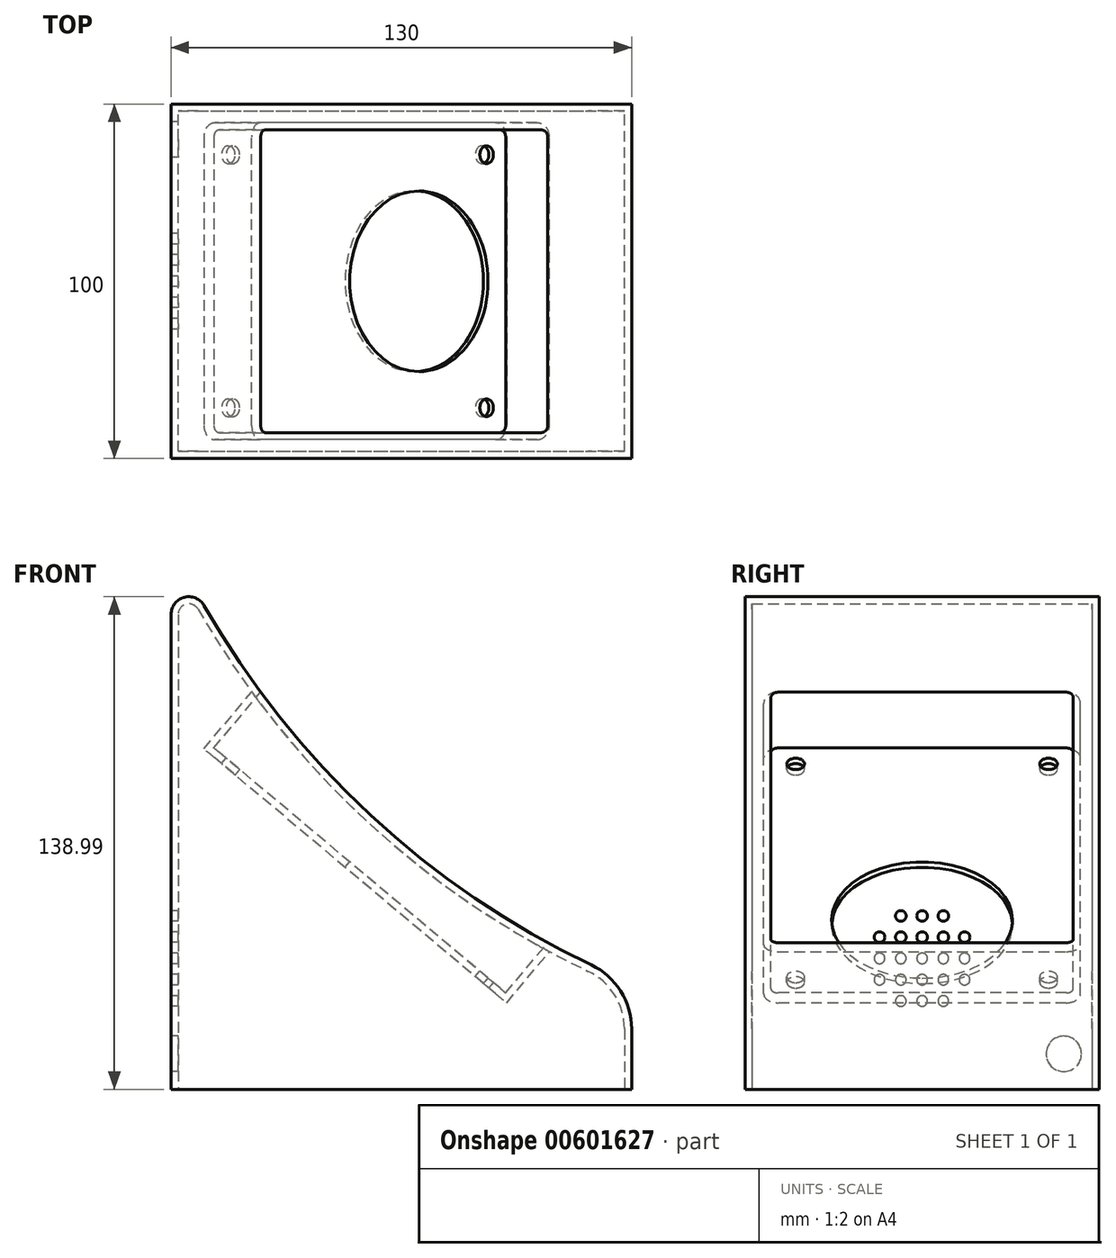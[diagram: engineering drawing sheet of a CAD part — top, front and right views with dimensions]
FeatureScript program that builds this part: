
annotation { "Feature Type Name" : "Feature", "Feature Type Description" : "" }
export const myFeature = defineFeature(function(context is Context, id is Id, definition is map)
    precondition{}
    {
        {
            var Q0;
            Q0=qCreatedBy(makeId("Front.planeOp"),FACE);
            var sketch = newSketch(context, id + "F0", { "sketchPlane" : qUnion([Q0])});
            skLineSegment(sketch, "E0", {"start": v(-84.02, -67.29) * mm, "end": v(45.98, -67.29) * mm});
            skPoint(sketch, "E1.visualSharp", {"position": v(-84.02, 87.14) * mm});
            skPoint(sketch, "E2.visualSharp", {"position": v(45.98, -37.29) * mm});
            skArc(sketch, "E3", {"start": v(-74.68, 69.19) * mm, "mid": v(-23.15, 5.98) * mm, "end": v(45.98, -37.29) * mm});
            skLineSegment(sketch, "E4", {"start": v(-84.02, 66.7) * mm, "end": v(-84.02, -67.29) * mm});
            skLineSegment(sketch, "E5", {"start": v(45.98, -37.29) * mm, "end": v(45.98, -67.29) * mm});
            skArc(sketch, "E6.filletArc", {"start": v(-74.68, 69.19) * mm, "mid": v(-80.3, 71.53) * mm, "end": v(-84.02, 66.7) * mm});
            skSolve(sketch);
        }
        {
            var Q0;
            Q0=makeQuery(id+"F0.imprint","IMPRINT",FACE,{"disambiguationData":[TD([[makeQuery(id+"F0.imprint","IMPRINT",EDGE,{"derivedFrom":sQuery(id+"F0.wireOp",EDGE,"E0")}),1.0]])]});
            extrude(context, id + "F1", {"entities" : qUnion([Q0]), "endBound" : BoundingType.SYMMETRIC, "depth" : 100 * mm});
        }
        {
            var Q0;
            Q0=makeQuery(id+"F1.opExtrude","SWEPT_EDGE",EDGE,{"disambiguationData":[OSD([sQuery(id+"F0.wireOp",EDGE,"E3"),sQuery(id+"F0.wireOp",EDGE,"E5")])]});
            cPlane(context, id + "F2", {"entities" : qUnion([Q0]), "cplaneType" : CPlaneType.LINE_ANGLE, "offset" : 25 * mm, "angle" : 40 * degree, "width" : 150 * mm, "height" : 150 * mm});
        }
        {
            var Q0;
            Q0=qCreatedBy(id+"F2.planeOp",FACE);
            var sketch = newSketch(context, id + "F3", { "sketchPlane" : qUnion([Q0])});
            skLineSegment(sketch, "E7.bottom", {"start": v(31.75, 42.7) * mm, "end": v(-71.75, 42.7) * mm});
            skLineSegment(sketch, "E7.top", {"start": v(31.75, -42.7) * mm, "end": v(-71.75, -42.7) * mm});
            skLineSegment(sketch, "E7.left", {"start": v(33.75, 40.7) * mm, "end": v(33.75, -40.7) * mm});
            skLineSegment(sketch, "E7.right", {"start": v(-73.75, 40.7) * mm, "end": v(-73.75, -40.7) * mm});
            skPoint(sketch, "E7.middle", {"position": v(-20, 0) * mm});
            skPoint(sketch, "E8.visualSharp", {"position": v(-73.75, -42.7) * mm});
            skArc(sketch, "E8.filletArc", {"start": v(-73.75, -40.7) * mm, "mid": v(-73.16, -42.11) * mm, "end": v(-71.75, -42.7) * mm});
            skPoint(sketch, "E9.visualSharp", {"position": v(-73.75, 42.7) * mm});
            skArc(sketch, "E9.filletArc", {"start": v(-71.75, 42.7) * mm, "mid": v(-73.16, 42.11) * mm, "end": v(-73.75, 40.7) * mm});
            skPoint(sketch, "E10.visualSharp", {"position": v(33.75, 42.7) * mm});
            skArc(sketch, "E10.filletArc", {"start": v(33.75, 40.7) * mm, "mid": v(33.16, 42.11) * mm, "end": v(31.75, 42.7) * mm});
            skPoint(sketch, "E11.visualSharp", {"position": v(33.75, -42.7) * mm});
            skArc(sketch, "E11.filletArc", {"start": v(31.75, -42.7) * mm, "mid": v(33.16, -42.11) * mm, "end": v(33.75, -40.7) * mm});
            skCircle(sketch, "E12", {"center": v(1.75, 0) * mm, "radius": 25.5 * mm});
            skCircle(sketch, "E13", {"center": v(-66.75, -35.7) * mm, "radius": 2.5 * mm});
            skCircle(sketch, "E14", {"center": v(-66.75, 35.7) * mm, "radius": 2.5 * mm});
            skCircle(sketch, "E15", {"center": v(26.75, 35.7) * mm, "radius": 2.5 * mm});
            skCircle(sketch, "E16", {"center": v(26.75, -35.7) * mm, "radius": 2.5 * mm});
            skSolve(sketch);
        }
        {
            var Q0;
            Q0=makeQuery(id+"F3.imprint","IMPRINT",FACE,{"disambiguationData":[TD([[makeQuery(id+"F3.imprint","IMPRINT",EDGE,{"derivedFrom":sQuery(id+"F3.wireOp",EDGE,"E7.bottom")}),1.0]])]});
            var Q1;
            Q1=makeQuery(id+"F3.imprint","IMPRINT",FACE,{"disambiguationData":[TD([[makeQuery(id+"F3.imprint","IMPRINT",EDGE,{"derivedFrom":sQuery(id+"F3.wireOp",EDGE,"E12")}),1.0]])]});
            var Q2;
            Q2=makeQuery(id+"F3.imprint","IMPRINT",FACE,{"disambiguationData":[TD([[makeQuery(id+"F3.imprint","IMPRINT",EDGE,{"derivedFrom":sQuery(id+"F3.wireOp",EDGE,"E14")}),1.0]])]});
            var Q3;
            Q3=makeQuery(id+"F3.imprint","IMPRINT",FACE,{"disambiguationData":[TD([[makeQuery(id+"F3.imprint","IMPRINT",EDGE,{"derivedFrom":sQuery(id+"F3.wireOp",EDGE,"E15")}),1.0]])]});
            var Q4;
            Q4=makeQuery(id+"F3.imprint","IMPRINT",FACE,{"disambiguationData":[TD([[makeQuery(id+"F3.imprint","IMPRINT",EDGE,{"derivedFrom":sQuery(id+"F3.wireOp",EDGE,"E16")}),1.0]])]});
            var Q5;
            Q5=makeQuery(id+"F3.imprint","IMPRINT",FACE,{"disambiguationData":[TD([[makeQuery(id+"F3.imprint","IMPRINT",EDGE,{"derivedFrom":sQuery(id+"F3.wireOp",EDGE,"E13")}),1.0]])]});
            extrude(context, id + "F4", {"entities" : qUnion([Q0, Q1, Q2, Q3, Q4, Q5]), "operationType" : NewBodyOperationType.REMOVE, "oppositeDirection" : true, "depth" : 25 * mm});
        }
        {
            var Q0;
            Q0=makeQuery(id+"F1.opExtrude","SWEPT_EDGE",EDGE,{"disambiguationData":[OSD([sQuery(id+"F0.wireOp",EDGE,"E3"),sQuery(id+"F0.wireOp",EDGE,"E5")])]});
            fillet(context, id + "F5", {"entities" : qUnion([Q0]), "radius" : 20 * mm, "tangentPropagation" : true, "allowEdgeOverflow" : false});
        }
        {
            var Q0;
            Q0=makeQuery(id+"F1.opExtrude","SWEPT_FACE",FACE,{"disambiguationData":[OSD([sQuery(id+"F0.wireOp",EDGE,"E0")])]});
            shell(context, id + "F6", {"entities" : qUnion([Q0]), "thickness" : 2 * mm});
        }
        {
            var Q0;
            Q0=makeQuery(id+"F3.imprint","IMPRINT",FACE,{"disambiguationData":[TD([[makeQuery(id+"F3.imprint","IMPRINT",EDGE,{"derivedFrom":sQuery(id+"F3.wireOp",EDGE,"E12")}),1.0]])]});
            var Q1;
            Q1=makeQuery(id+"F3.imprint","IMPRINT",FACE,{"disambiguationData":[TD([[makeQuery(id+"F3.imprint","IMPRINT",EDGE,{"derivedFrom":sQuery(id+"F3.wireOp",EDGE,"E14")}),1.0]])]});
            var Q2;
            Q2=makeQuery(id+"F3.imprint","IMPRINT",FACE,{"disambiguationData":[TD([[makeQuery(id+"F3.imprint","IMPRINT",EDGE,{"derivedFrom":sQuery(id+"F3.wireOp",EDGE,"E13")}),1.0]])]});
            var Q3;
            Q3=makeQuery(id+"F3.imprint","IMPRINT",FACE,{"disambiguationData":[TD([[makeQuery(id+"F3.imprint","IMPRINT",EDGE,{"derivedFrom":sQuery(id+"F3.wireOp",EDGE,"E15")}),1.0]])]});
            var Q4;
            Q4=makeQuery(id+"F3.imprint","IMPRINT",FACE,{"disambiguationData":[TD([[makeQuery(id+"F3.imprint","IMPRINT",EDGE,{"derivedFrom":sQuery(id+"F3.wireOp",EDGE,"E16")}),1.0]])]});
            extrude(context, id + "F7", {"entities" : qUnion([Q0, Q1, Q2, Q3, Q4]), "operationType" : NewBodyOperationType.REMOVE, "oppositeDirection" : true, "depth" : 40 * mm});
        }
        {
            var Q0;
            Q0=makeQuery(id+"F1.opExtrude","SWEPT_FACE",FACE,{"disambiguationData":[OSD([sQuery(id+"F0.wireOp",EDGE,"E4")])]});
            var sketch = newSketch(context, id + "F8", { "sketchPlane" : qUnion([Q0])});
            skCircle(sketch, "E17", {"center": v(0, -30.36) * mm, "radius": 25 * mm, "construction": true});
            skLineSegment(sketch, "E18", {"start": v(0, 0) * mm, "end": v(0, -62.03) * mm, "construction": true});
            skLineSegment(sketch, "E19", {"start": v(-40.29, -30.36) * mm, "end": v(40.58, -30.36) * mm, "construction": true});
            skLineSegment(sketch, "E20", {"start": v(-40.29, -24.36) * mm, "end": v(40.58, -24.36) * mm, "construction": true});
            skLineSegment(sketch, "E21", {"start": v(-40.29, -36.36) * mm, "end": v(40.58, -36.36) * mm, "construction": true});
            skLineSegment(sketch, "E22", {"start": v(-40.29, -42.36) * mm, "end": v(40.58, -42.36) * mm, "construction": true});
            skLineSegment(sketch, "E23", {"start": v(-40.29, -18.36) * mm, "end": v(40.58, -18.36) * mm, "construction": true});
            skLineSegment(sketch, "E24", {"start": v(-6, 0) * mm, "end": v(-6, -62.03) * mm, "construction": true});
            skLineSegment(sketch, "E25", {"start": v(6, 0) * mm, "end": v(6, -62.03) * mm, "construction": true});
            skLineSegment(sketch, "E26", {"start": v(12, 0) * mm, "end": v(12, -62.03) * mm, "construction": true});
            skLineSegment(sketch, "E27", {"start": v(-12, 0) * mm, "end": v(-12, -62.03) * mm, "construction": true});
            skCircle(sketch, "E28", {"center": v(0, -30.36) * mm, "radius": 1.5 * mm});
            skCircle(sketch, "E29", {"center": v(6, -30.36) * mm, "radius": 1.5 * mm});
            skCircle(sketch, "E30", {"center": v(12, -30.36) * mm, "radius": 1.5 * mm});
            skCircle(sketch, "E31", {"center": v(-6, -30.36) * mm, "radius": 1.5 * mm});
            skCircle(sketch, "E32", {"center": v(-12, -30.36) * mm, "radius": 1.5 * mm});
            skCircle(sketch, "E33", {"center": v(0, -24.36) * mm, "radius": 1.5 * mm});
            skCircle(sketch, "E34", {"center": v(6, -24.36) * mm, "radius": 1.5 * mm});
            skCircle(sketch, "E35", {"center": v(-6, -24.36) * mm, "radius": 1.5 * mm});
            skCircle(sketch, "E36", {"center": v(-6, -18.36) * mm, "radius": 1.5 * mm});
            skCircle(sketch, "E37", {"center": v(0, -18.36) * mm, "radius": 1.5 * mm});
            skCircle(sketch, "E38", {"center": v(6, -18.36) * mm, "radius": 1.5 * mm});
            skCircle(sketch, "E39", {"center": v(12, -24.36) * mm, "radius": 1.5 * mm});
            skCircle(sketch, "E40", {"center": v(12, -36.36) * mm, "radius": 1.5 * mm});
            skCircle(sketch, "E41", {"center": v(6, -36.36) * mm, "radius": 1.5 * mm});
            skCircle(sketch, "E42", {"center": v(0, -36.36) * mm, "radius": 1.5 * mm});
            skCircle(sketch, "E43", {"center": v(-6, -36.36) * mm, "radius": 1.5 * mm});
            skCircle(sketch, "E44", {"center": v(-12, -36.36) * mm, "radius": 1.5 * mm});
            skCircle(sketch, "E45", {"center": v(-6, -42.36) * mm, "radius": 1.5 * mm});
            skCircle(sketch, "E46", {"center": v(0, -42.36) * mm, "radius": 1.5 * mm});
            skCircle(sketch, "E47", {"center": v(6, -42.36) * mm, "radius": 1.5 * mm});
            skCircle(sketch, "E48", {"center": v(-12, -24.36) * mm, "radius": 1.5 * mm});
            skCircle(sketch, "E49", {"center": v(-40, -57.29) * mm, "radius": 5 * mm});
            skSolve(sketch);
        }
        {
            var Q0;
            Q0=makeQuery(id+"F8.imprint","IMPRINT",FACE,{"disambiguationData":[TD([[makeQuery(id+"F8.imprint","IMPRINT",EDGE,{"derivedFrom":sQuery(id+"F8.wireOp",EDGE,"E36")}),1.0]])]});
            var Q1;
            Q1=makeQuery(id+"F8.imprint","IMPRINT",FACE,{"disambiguationData":[TD([[makeQuery(id+"F8.imprint","IMPRINT",EDGE,{"derivedFrom":sQuery(id+"F8.wireOp",EDGE,"E37")}),1.0]])]});
            var Q2;
            Q2=makeQuery(id+"F8.imprint","IMPRINT",FACE,{"disambiguationData":[TD([[makeQuery(id+"F8.imprint","IMPRINT",EDGE,{"derivedFrom":sQuery(id+"F8.wireOp",EDGE,"E38")}),1.0]])]});
            var Q3;
            Q3=makeQuery(id+"F8.imprint","IMPRINT",FACE,{"disambiguationData":[TD([[makeQuery(id+"F8.imprint","IMPRINT",EDGE,{"derivedFrom":sQuery(id+"F8.wireOp",EDGE,"E39")}),1.0]])]});
            var Q4;
            Q4=makeQuery(id+"F8.imprint","IMPRINT",FACE,{"disambiguationData":[TD([[makeQuery(id+"F8.imprint","IMPRINT",EDGE,{"derivedFrom":sQuery(id+"F8.wireOp",EDGE,"E34")}),1.0]])]});
            var Q5;
            Q5=makeQuery(id+"F8.imprint","IMPRINT",FACE,{"disambiguationData":[TD([[makeQuery(id+"F8.imprint","IMPRINT",EDGE,{"derivedFrom":sQuery(id+"F8.wireOp",EDGE,"E33")}),1.0]])]});
            var Q6;
            Q6=makeQuery(id+"F8.imprint","IMPRINT",FACE,{"disambiguationData":[TD([[makeQuery(id+"F8.imprint","IMPRINT",EDGE,{"derivedFrom":sQuery(id+"F8.wireOp",EDGE,"E35")}),1.0]])]});
            var Q7;
            Q7=makeQuery(id+"F8.imprint","IMPRINT",FACE,{"disambiguationData":[TD([[makeQuery(id+"F8.imprint","IMPRINT",EDGE,{"derivedFrom":sQuery(id+"F8.wireOp",EDGE,"E48")}),1.0]])]});
            var Q8;
            Q8=makeQuery(id+"F8.imprint","IMPRINT",FACE,{"disambiguationData":[TD([[makeQuery(id+"F8.imprint","IMPRINT",EDGE,{"derivedFrom":sQuery(id+"F8.wireOp",EDGE,"E32")}),1.0]])]});
            var Q9;
            Q9=makeQuery(id+"F8.imprint","IMPRINT",FACE,{"disambiguationData":[TD([[makeQuery(id+"F8.imprint","IMPRINT",EDGE,{"derivedFrom":sQuery(id+"F8.wireOp",EDGE,"E31")}),1.0]])]});
            var Q10;
            Q10=makeQuery(id+"F8.imprint","IMPRINT",FACE,{"disambiguationData":[TD([[makeQuery(id+"F8.imprint","IMPRINT",EDGE,{"derivedFrom":sQuery(id+"F8.wireOp",EDGE,"E28")}),1.0]])]});
            var Q11;
            Q11=makeQuery(id+"F8.imprint","IMPRINT",FACE,{"disambiguationData":[TD([[makeQuery(id+"F8.imprint","IMPRINT",EDGE,{"derivedFrom":sQuery(id+"F8.wireOp",EDGE,"E29")}),1.0]])]});
            var Q12;
            Q12=makeQuery(id+"F8.imprint","IMPRINT",FACE,{"disambiguationData":[TD([[makeQuery(id+"F8.imprint","IMPRINT",EDGE,{"derivedFrom":sQuery(id+"F8.wireOp",EDGE,"E30")}),1.0]])]});
            var Q13;
            Q13=makeQuery(id+"F8.imprint","IMPRINT",FACE,{"disambiguationData":[TD([[makeQuery(id+"F8.imprint","IMPRINT",EDGE,{"derivedFrom":sQuery(id+"F8.wireOp",EDGE,"E41")}),1.0]])]});
            var Q14;
            Q14=makeQuery(id+"F8.imprint","IMPRINT",FACE,{"disambiguationData":[TD([[makeQuery(id+"F8.imprint","IMPRINT",EDGE,{"derivedFrom":sQuery(id+"F8.wireOp",EDGE,"E42")}),1.0]])]});
            var Q15;
            Q15=makeQuery(id+"F8.imprint","IMPRINT",FACE,{"disambiguationData":[TD([[makeQuery(id+"F8.imprint","IMPRINT",EDGE,{"derivedFrom":sQuery(id+"F8.wireOp",EDGE,"E43")}),1.0]])]});
            var Q16;
            Q16=makeQuery(id+"F8.imprint","IMPRINT",FACE,{"disambiguationData":[TD([[makeQuery(id+"F8.imprint","IMPRINT",EDGE,{"derivedFrom":sQuery(id+"F8.wireOp",EDGE,"E44")}),1.0]])]});
            var Q17;
            Q17=makeQuery(id+"F8.imprint","IMPRINT",FACE,{"disambiguationData":[TD([[makeQuery(id+"F8.imprint","IMPRINT",EDGE,{"derivedFrom":sQuery(id+"F8.wireOp",EDGE,"E45")}),1.0]])]});
            var Q18;
            Q18=makeQuery(id+"F8.imprint","IMPRINT",FACE,{"disambiguationData":[TD([[makeQuery(id+"F8.imprint","IMPRINT",EDGE,{"derivedFrom":sQuery(id+"F8.wireOp",EDGE,"E46")}),1.0]])]});
            var Q19;
            Q19=makeQuery(id+"F8.imprint","IMPRINT",FACE,{"disambiguationData":[TD([[makeQuery(id+"F8.imprint","IMPRINT",EDGE,{"derivedFrom":sQuery(id+"F8.wireOp",EDGE,"E47")}),1.0]])]});
            var Q20;
            Q20=makeQuery(id+"F8.imprint","IMPRINT",FACE,{"disambiguationData":[TD([[makeQuery(id+"F8.imprint","IMPRINT",EDGE,{"derivedFrom":sQuery(id+"F8.wireOp",EDGE,"E40")}),1.0]])]});
            var Q21;
            Q21=makeQuery(id+"F8.imprint","IMPRINT",FACE,{"disambiguationData":[TD([[makeQuery(id+"F8.imprint","IMPRINT",EDGE,{"derivedFrom":sQuery(id+"F8.wireOp",EDGE,"E49")}),1.0]])]});
            var Q22;
            Q22=sQuery(id+"F8.wireOp",EDGE,"E48");
            var Q23;
            Q23=sQuery(id+"F8.wireOp",EDGE,"E35");
            var Q24;
            Q24=sQuery(id+"F8.wireOp",EDGE,"E36");
            var Q25;
            Q25=sQuery(id+"F8.wireOp",EDGE,"E37");
            var Q26;
            Q26=sQuery(id+"F8.wireOp",EDGE,"E38");
            var Q27;
            Q27=sQuery(id+"F8.wireOp",EDGE,"E34");
            var Q28;
            Q28=sQuery(id+"F8.wireOp",EDGE,"E33");
            var Q29;
            Q29=sQuery(id+"F8.wireOp",EDGE,"E39");
            var Q30;
            Q30=sQuery(id+"F8.wireOp",EDGE,"E30");
            var Q31;
            Q31=sQuery(id+"F8.wireOp",EDGE,"E29");
            var Q32;
            Q32=sQuery(id+"F8.wireOp",EDGE,"E28");
            var Q33;
            Q33=sQuery(id+"F8.wireOp",EDGE,"E31");
            var Q34;
            Q34=sQuery(id+"F8.wireOp",EDGE,"E32");
            var Q35;
            Q35=sQuery(id+"F8.wireOp",EDGE,"E44");
            var Q36;
            Q36=sQuery(id+"F8.wireOp",EDGE,"E43");
            var Q37;
            Q37=sQuery(id+"F8.wireOp",EDGE,"E42");
            var Q38;
            Q38=sQuery(id+"F8.wireOp",EDGE,"E41");
            var Q39;
            Q39=sQuery(id+"F8.wireOp",EDGE,"E40");
            var Q40;
            Q40=sQuery(id+"F8.wireOp",EDGE,"E47");
            var Q41;
            Q41=sQuery(id+"F8.wireOp",EDGE,"E46");
            var Q42;
            Q42=sQuery(id+"F8.wireOp",EDGE,"E45");
            extrude(context, id + "F9", {"entities" : qUnion([Q0, Q1, Q2, Q3, Q4, Q5, Q6, Q7, Q8, Q9, Q10, Q11, Q12, Q13, Q14, Q15, Q16, Q17, Q18, Q19, Q20, Q21]), "operationType" : NewBodyOperationType.REMOVE, "surfaceEntities" : qUnion([Q22, Q23, Q24, Q25, Q26, Q27, Q28, Q29, Q30, Q31, Q32, Q33, Q34, Q35, Q36, Q37, Q38, Q39, Q40, Q41, Q42]), "oppositeDirection" : true, "depth" : 25 * mm});
        }
    });
